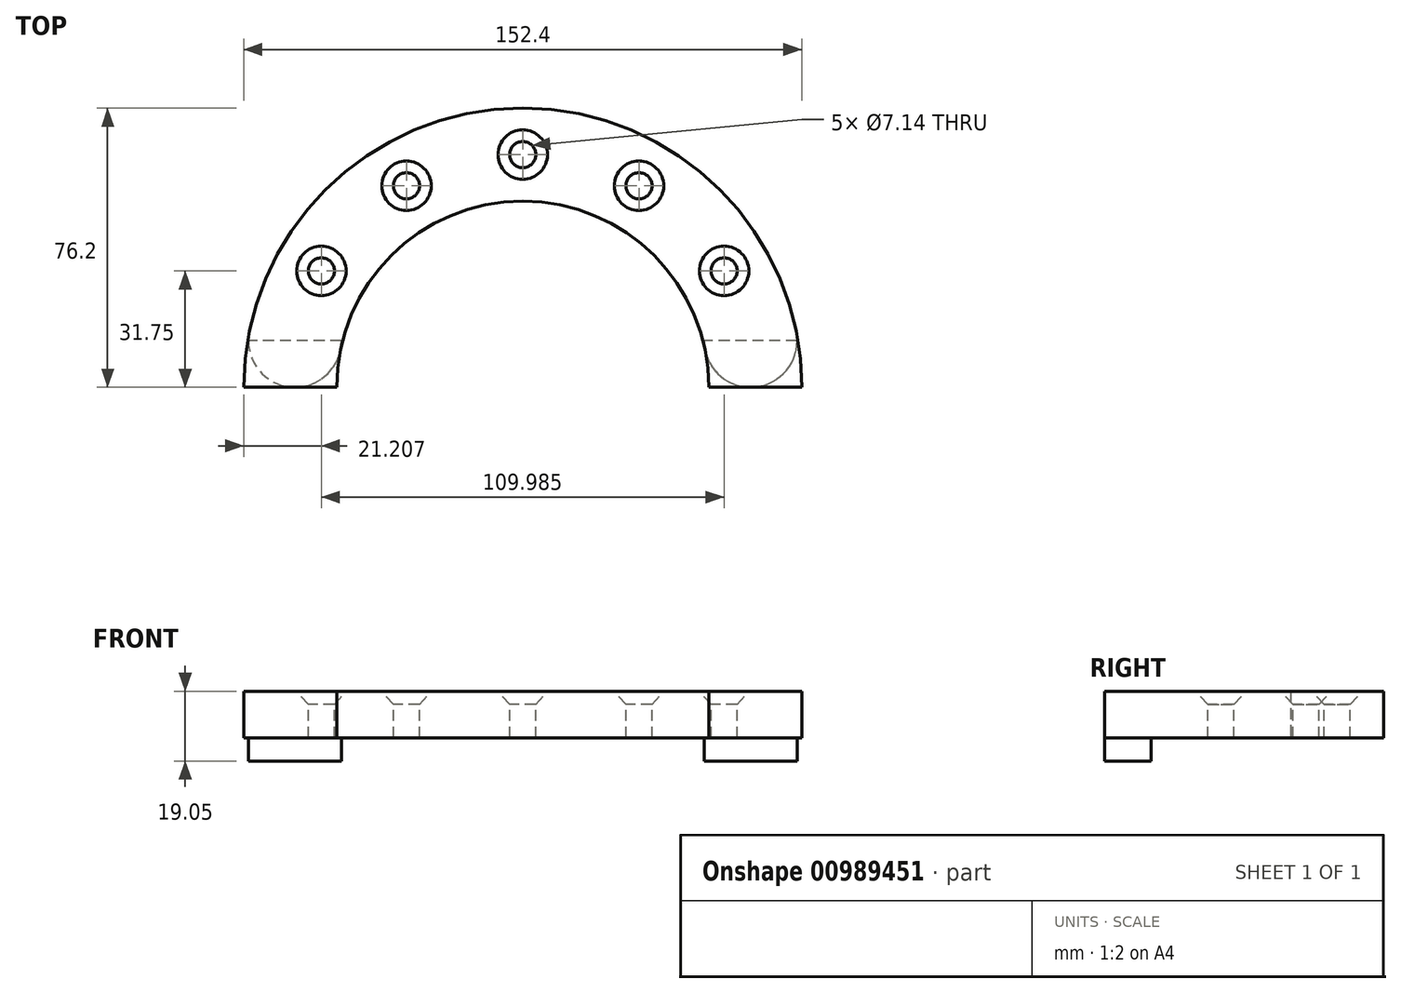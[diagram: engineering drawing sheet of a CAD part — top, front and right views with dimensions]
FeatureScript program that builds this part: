
annotation { "Feature Type Name" : "Feature", "Feature Type Description" : "" }
export const myFeature = defineFeature(function(context is Context, id is Id, definition is map)
    precondition{}
    {
        {
            var Q0;
            Q0=qCreatedBy(makeId("Top.planeOp"),FACE);
            var sketch = newSketch(context, id + "F0", { "sketchPlane" : qUnion([Q0])});
            skArc(sketch, "E0", {"start": v(-50.8, 0) * mm, "mid": v(0, 50.8) * mm, "end": v(50.8, 0) * mm});
            skArc(sketch, "E1", {"start": v(76.2, 0) * mm, "mid": v(0, 76.2) * mm, "end": v(-76.2, 0) * mm});
            skLineSegment(sketch, "E2", {"start": v(-76.2, 0) * mm, "end": v(-50.8, 0) * mm});
            skLineSegment(sketch, "E3", {"start": v(50.8, 0) * mm, "end": v(76.2, 0) * mm});
            skSolve(sketch);
        }
        {
            var Q0;
            Q0 = qSketchRegion(id + "F0", true);
            extrude(context, id + "F1", {"entities" : qUnion([Q0]), "depth" : 12.7 * mm, "offsetDistance" : 25.4 * mm});
        }
        {
            var Q0;
            Q0=makeQuery(id+"F1.opExtrude","CAP_FACE",FACE,{"disambiguationData":[OSD([sQuery(id+"F0.wireOp",EDGE,"E0"),sQuery(id+"F0.wireOp",EDGE,"E1"),sQuery(id+"F0.wireOp",EDGE,"E2"),sQuery(id+"F0.wireOp",EDGE,"E3")])],"isStart":true});
            var sketch = newSketch(context, id + "F2", { "sketchPlane" : qUnion([Q0])});
            skArc(sketch, "E4", {"start": v(-49.52, -12.7) * mm, "mid": v(-62.22, 0) * mm, "end": v(-74.92, -12.7) * mm});
            skLineSegment(sketch, "E5", {"start": v(-62.22, -12.7) * mm, "end": v(-74.92, -12.7) * mm});
            skLineSegment(sketch, "E6", {"start": v(-62.22, -12.7) * mm, "end": v(-49.52, -12.7) * mm});
            skLineSegment(sketch, "E7", {"start": v(0, 0) * mm, "end": v(0, -88.85) * mm, "construction": true});
            skArc(sketch, "E8.MirrorCS", {"start": v(49.52, -12.7) * mm, "mid": v(62.22, 0) * mm, "end": v(74.92, -12.7) * mm});
            skLineSegment(sketch, "E9.MirrorCS", {"start": v(62.22, -12.7) * mm, "end": v(49.52, -12.7) * mm});
            skLineSegment(sketch, "E10.MirrorCS", {"start": v(62.22, -12.7) * mm, "end": v(74.92, -12.7) * mm});
            skSolve(sketch);
        }
        {
            var Q0;
            Q0 = qSketchRegion(id + "F2", true);
            extrude(context, id + "F3", {"entities" : qUnion([Q0]), "operationType" : NewBodyOperationType.ADD, "depth" : 6.35 * mm, "offsetDistance" : 25.4 * mm});
        }
        {
            var Q0;
            Q0=makeQuery(id+"F1.opExtrude","CAP_FACE",FACE,{"disambiguationData":[OSD([sQuery(id+"F0.wireOp",EDGE,"E0"),sQuery(id+"F0.wireOp",EDGE,"E1"),sQuery(id+"F0.wireOp",EDGE,"E2"),sQuery(id+"F0.wireOp",EDGE,"E3")])],"isStart":false});
            var sketch = newSketch(context, id + "F4", { "sketchPlane" : qUnion([Q0])});
            skArc(sketch, "E11", {"start": v(-63.5, 0) * mm, "mid": v(0, 63.5) * mm, "end": v(63.5, 0) * mm, "construction": true});
            skPoint(sketch, "E12", {"position": v(-63.5, 0) * mm});
            skPoint(sketch, "E13.1.0", {"position": v(-55, 31.75) * mm});
            skPoint(sketch, "E13.2.0", {"position": v(-31.75, 55) * mm});
            skPoint(sketch, "E13.3.0", {"position": v(0, 63.5) * mm});
            skPoint(sketch, "E13.4.0", {"position": v(31.75, 55) * mm});
            skPoint(sketch, "E13.5.0", {"position": v(55, 31.75) * mm});
            skPoint(sketch, "E13.6.0", {"position": v(63.5, 0) * mm});
            skLineSegment(sketch, "E13.anchor1", {"start": v(0, 0) * mm, "end": v(-63.5, 0) * mm, "construction": true});
            skLineSegment(sketch, "E13.anchor2", {"start": v(0, 0) * mm, "end": v(63.5, 0) * mm, "construction": true});
            skSolve(sketch);
        }
        {
            var Q0;
            Q0=sQuery(id+"F4.wireOp",VERTEX,"E13.1.0");
            var Q1;
            Q1=sQuery(id+"F4.wireOp",VERTEX,"E13.2.0");
            var Q2;
            Q2=sQuery(id+"F4.wireOp",VERTEX,"E13.3.0");
            var Q3;
            Q3=sQuery(id+"F4.wireOp",VERTEX,"E13.4.0");
            var Q4;
            Q4=sQuery(id+"F4.wireOp",VERTEX,"E13.5.0");
            var Q5;
            Q5=makeQuery(id+"F1.opExtrude","SWEPT_BODY",BODY,{"disambiguationData":[OSD([sQuery(id+"F0.wireOp",EDGE,"E0"),sQuery(id+"F0.wireOp",EDGE,"E1"),sQuery(id+"F0.wireOp",EDGE,"E2"),sQuery(id+"F0.wireOp",EDGE,"E3")])]});
            hole(context, id + "F5", {"style" : HoleStyle.C_SINK, "endStyle" : HoleEndStyle.THROUGH, "standardTappedOrClearance" : lookupTablePath({ "fit" : "Normal (ASME)", "standard" : "ANSI", "size" : "1/4", "type" : "Clearance" }), "standardBlindInLast" : lookupTablePath({ "fit" : "Normal", "standard" : "ANSI", "engagement" : "75%", "pitch" : "20 tpi", "size" : "1/4", "type" : "Clearance & tapped" }), "holeDiameter" : 7.14 * mm, "cSinkDiameter" : 13.5 * mm, "cSinkAngle" : 82 * degree, "majorDiameter" : 6.35 * mm, "isTappedThrough" : true, "tappedDepth" : 12.7 * mm, "tapClearance" : 3, "locations" : qUnion([Q0, Q1, Q2, Q3, Q4]), "scope" : qUnion([Q5])});
        }
    });
